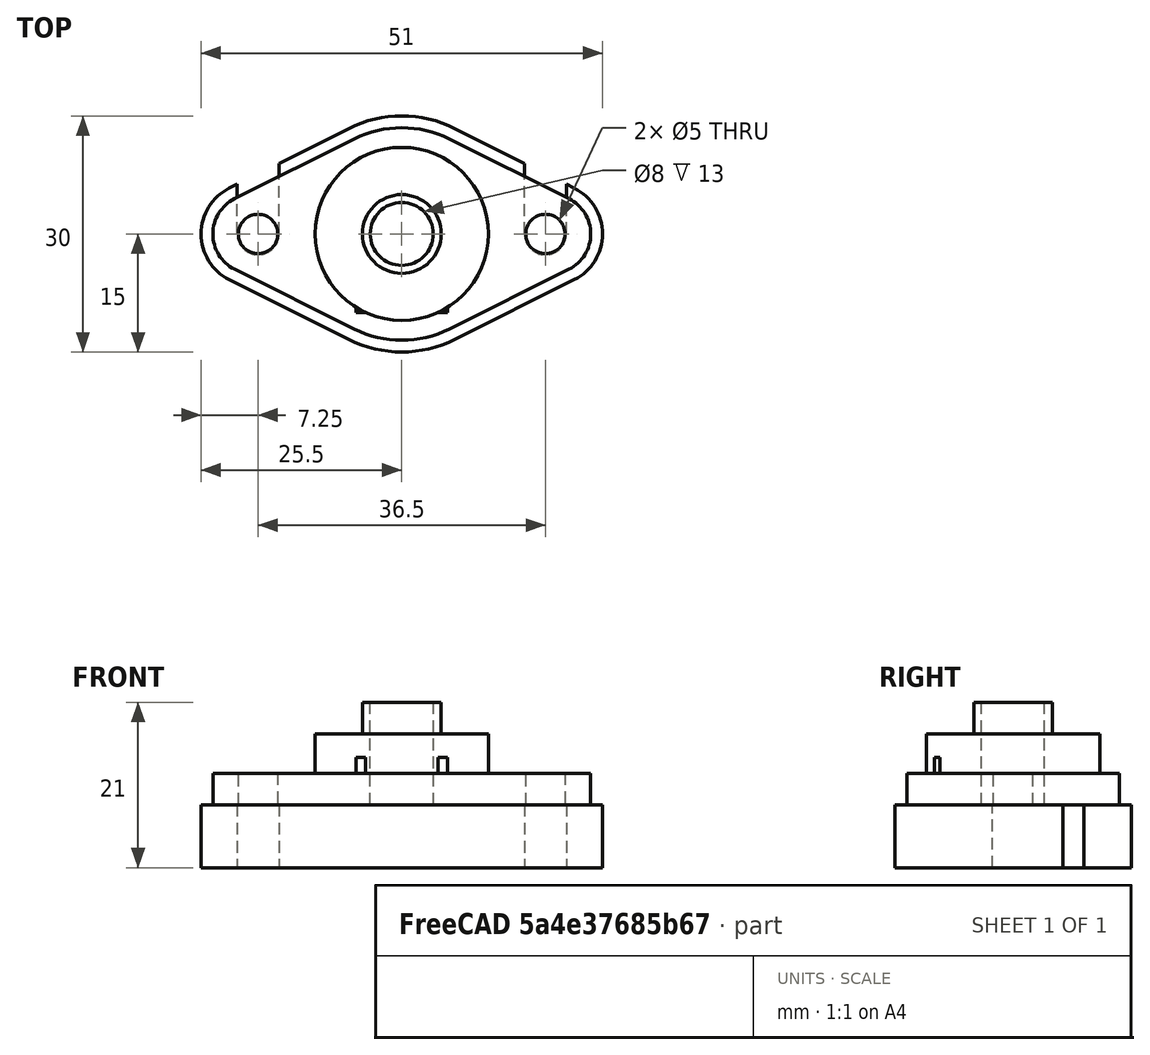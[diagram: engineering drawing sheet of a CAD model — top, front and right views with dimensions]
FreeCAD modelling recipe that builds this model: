
FCSTD DOCUMENT  (FreeCAD 0.20R26683 (Git))
Label: KFL08 spacer
License: All rights reserved
LicenseURL: http://en.wikipedia.org/wiki/All_rights_reserved
objects: Part::Feature×1, PartDesign::SubShapeBinder×1, Sketcher::SketchObject×1, PartDesign::Pad×1, PartDesign::Body×1
note: 6 computed .brp shape members not serialized (recipe doc carries the construction recipe); baked Part::Feature solids carry a one-line shape summary decoded from their .brp

FEATURE [Part::Feature] Part__Feature  label="Body001"
  shape: bbox 48 x 27 x 13 mm, 23 faces (baked)
FEATURE [PartDesign::SubShapeBinder] Binder
  BindMode = 0
  ClaimChildren = false
  Context = -> Body [Binder.]
  Fuse = false
  MakeFace = true
  PartialLoad = false
  Relative = true
  Support = -> [Part__Feature]
  _Version = 2
FEATURE [Sketcher::SketchObject] Sketch
  ExternalGeometry = -> [Binder]
  FullyConstrained = true
  MapMode = 5
  Placement = pos=(0,0,0) rot=(1,0,0;3.14159rad)
  Support = -> [Binder]
  sketch-geometry (18):
    g0: ArcOfCircle CenterX=-19 CenterY=0 CenterZ=0 NormalX=0 NormalY=0 NormalZ=1 AngleXU=0 Radius=6.5 StartAngle=2.03462 EndAngle=4.24857
    g1: ArcOfCircle CenterX=0 CenterY=0 CenterZ=0 NormalX=0 NormalY=0 NormalZ=1 AngleXU=0 Radius=15 StartAngle=1.10698 EndAngle=2.03462
    g2: ArcOfCircle CenterX=19 CenterY=0 CenterZ=0 NormalX=0 NormalY=0 NormalZ=1 AngleXU=0 Radius=6.5 StartAngle=5.17621 EndAngle=7.39016
    g3: ArcOfCircle CenterX=0 CenterY=0 CenterZ=0 NormalX=0 NormalY=0 NormalZ=1 AngleXU=0 Radius=15 StartAngle=4.24857 EndAngle=5.17621
    g4: LineSegment StartX=-21.9079 StartY=5.81327 StartZ=0 EndX=-6.71053 EndY=13.4152 EndZ=0
    g5: LineSegment StartX=6.71053 StartY=13.4152 StartZ=0 EndX=21.9079 EndY=5.81327 EndZ=0
    g6: ArcOfCircle CenterX=-18.25 CenterY=0 CenterZ=0 NormalX=0 NormalY=0 NormalZ=1 AngleXU=0 Radius=2.65 StartAngle=0 EndAngle=3.14159
    g7: ArcOfCircle CenterX=18.25 CenterY=0 CenterZ=0 NormalX=0 NormalY=0 NormalZ=1 AngleXU=0 Radius=2.65 StartAngle=0 EndAngle=3.14159
    g8: LineSegment StartX=-20.9 StartY=3e-16 StartZ=0 EndX=-20.9 EndY=-6.31744 EndZ=0
    g9: LineSegment StartX=-15.6 StartY=0 StartZ=0 EndX=-15.6 EndY=-8.96859 EndZ=0
    g10: LineSegment StartX=-6.71053 StartY=-13.4152 StartZ=0 EndX=-15.6 EndY=-8.96859 EndZ=0
    g11: LineSegment StartX=15.6 StartY=3e-16 StartZ=0 EndX=15.6 EndY=-8.96859 EndZ=0
    g12: LineSegment StartX=6.71053 StartY=-13.4152 StartZ=0 EndX=15.6 EndY=-8.96859 EndZ=0
    g13: LineSegment StartX=20.9 StartY=0 StartZ=0 EndX=20.9 EndY=-6.31744 EndZ=0
    g14: LineSegment StartX=-21.9079 StartY=-5.81327 StartZ=0 EndX=-20.9 EndY=-6.31744 EndZ=0
    g15: LineSegment StartX=20.9 StartY=-6.31744 StartZ=0 EndX=21.9079 EndY=-5.81327 EndZ=0
    g16: LineSegment StartX=-25.5 StartY=0 StartZ=0 EndX=-24 EndY=0 EndZ=0
    g17: LineSegment StartX=0 StartY=15 StartZ=0 EndX=0 EndY=13.5 EndZ=0
  constraints (48):
    c: Coincident(g0,g-4)
    c: Coincident(g1,g-1)
    c: Coincident(g2,g-3)
    c: Coincident(g3,g1)
    c: Coincident(g6,g-5)
    c: PointOnObject(g6,g-1)
    c: PointOnObject(g6,g-1)
    c: Coincident(g7,g-6)
    c: PointOnObject(g7,g-1)
    c: PointOnObject(g7,g-1)
    c: Coincident(g8,g6)
    c: Vertical(g8)
    c: Diameter(g6) = 5.3
    c: Coincident(g9,g6)
    c: Vertical(g9)
    c: Coincident(g10,g9)
    c: Tangent(g10,g3) = 1.5708
    c: Equal(g6,g7)
    c: Coincident(g11,g7)
    c: Vertical(g11)
    c: Coincident(g12,g11)
    c: Tangent(g12,g3) = -1.5708
    c: Vertical(g3,g1)
    c: Vertical(g1,g3)
    c: Tangent(g4,g1) = 1.5708
    c: Tangent(g5,g1) = 1.5708
    c: Tangent(g5,g2) = 1.5708
    c: Coincident(g13,g7)
    c: Vertical(g13)
    c: Equal(g2,g0)
    c: Tangent(g4,g0) = 1.5708
    c: Equal(g3,g1)
    c: Coincident(g14,g8)
    c: Tangent(g14,g0) = -1.5708
    c: Coincident(g15,g13)
    c: Tangent(g15,g2) = -1.5708
    c: Equal(g15,g14)
    c: PointOnObject(g16,g0)
    c: PointOnObject(g16,g-4)
    c: Horizontal(g16)
    c: PointOnObject(g16,g-1)
    c: DistanceX(g16,g16) = 1.5
    c: Parallel(g14,g10)
    c: PointOnObject(g17,g1)
    c: PointOnObject(g17,g-7)
    c: Vertical(g17)
    c: PointOnObject(g17,g-2)
    c: Equal(g16,g17)
FEATURE [PartDesign::Pad] Pad
  Direction = (0,0,-1)
  Length = 8
  Length2 = 100
  Profile = -> Sketch
  ReferenceAxis = -> Sketch [N_Axis]
  Refine = true
  Type = 0
FEATURE [PartDesign::Body] Body
  Group = -> [Binder,Sketch,Pad]
  Origin = -> Origin
  Tip = -> Pad
